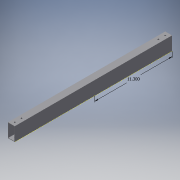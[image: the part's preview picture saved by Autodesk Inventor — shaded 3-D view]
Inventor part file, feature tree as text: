
AUTODESK INVENTOR PART (.ipt)
format: ipt  version: 2018 (Build 220112000, 112)  size: 140,288 bytes
history: native  units: in
note: dims shown in document units (in); Inventor stores cm internally (conversion verified against a paired STEP export)
features: extrude x4, sketch x4
ambient origin geometry x8: Origin, YZ Plane, XZ Plane, XY Plane, X Axis, Y Axis, Z Axis, Center Point
bodies: Solid1 (feature_tree)
feature tree (8):
  extrude  "Extrusion1"  Depth=2.0in
  extrude  "Extrusion2"  Depth=23.0in TaperAngle=0.0deg
  extrude  "Extrusion4"  Depth=0.5in
  extrude  "Extrusion5"  Depth=1.0in TaperAngle=0.0deg
  sketch  "Sketch1"  dims[d0=1.0in d1=2.0in]
  sketch  "Sketch2"  dims[d2=0.0625in d3=23.0in d4=0.0in]
  sketch  "Sketch3"  dims[d5=0.5in d6=0.5in]
  sketch  "Sketch4"  dims[d7=0.2031in d8=28.0in d9=0.0in d10=1.0in d13=1.0in d14=2.6875in d15=0.0in d16=11.1875in d17=2.0in d18=0.5in d19=1.0in d20=1.0in d21=0.2031in d22=0.2031in d23=1.0in d24=0.0in]
